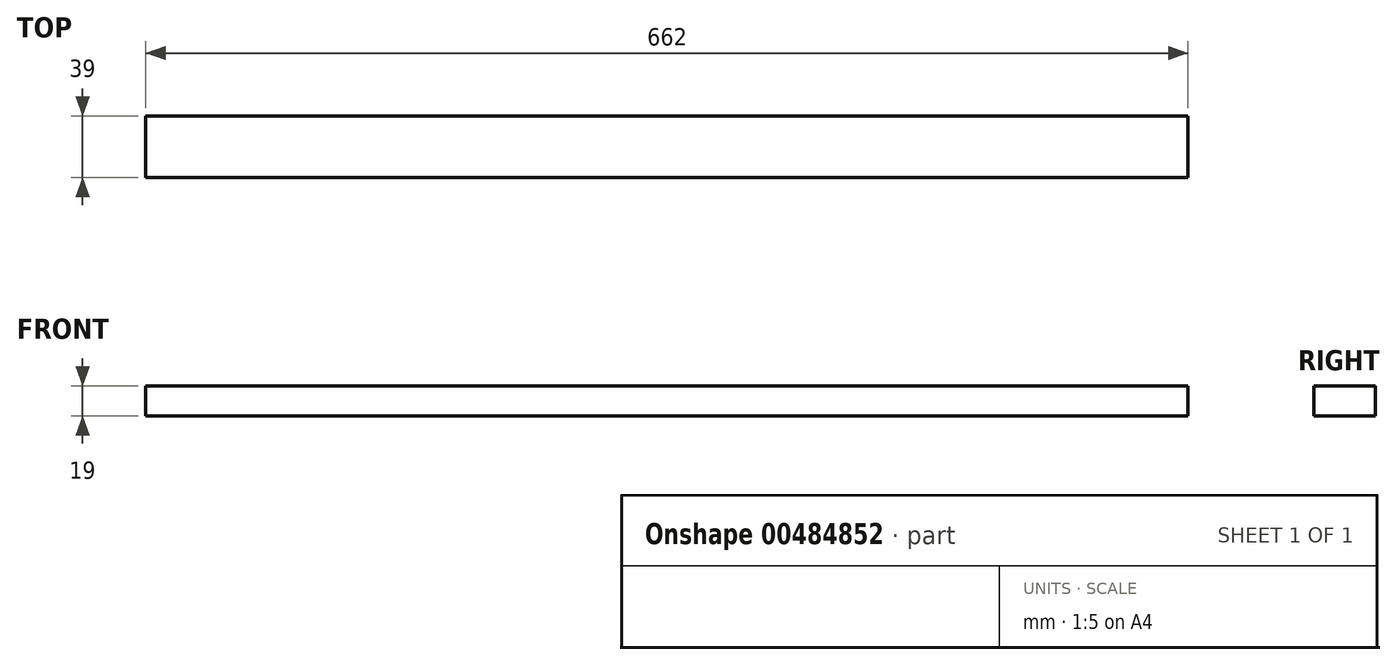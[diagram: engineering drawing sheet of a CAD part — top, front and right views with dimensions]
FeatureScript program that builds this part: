
annotation { "Feature Type Name" : "Feature", "Feature Type Description" : "" }
export const myFeature = defineFeature(function(context is Context, id is Id, definition is map)
    precondition{}
    {
        {
            var Q0;
            Q0=qCreatedBy(makeId("Top.planeOp"),FACE);
            var sketch = newSketch(context, id + "F0", { "sketchPlane" : qUnion([Q0])});
            skLineSegment(sketch, "E0.bottom", {"start": v(-202.57, 4.24) * mm, "end": v(459.43, 4.24) * mm});
            skLineSegment(sketch, "E0.top", {"start": v(-202.57, -34.76) * mm, "end": v(459.43, -34.76) * mm});
            skLineSegment(sketch, "E0.left", {"start": v(-202.57, 4.24) * mm, "end": v(-202.57, -34.76) * mm});
            skLineSegment(sketch, "E0.right", {"start": v(459.43, 4.24) * mm, "end": v(459.43, -34.76) * mm});
            skSolve(sketch);
        }
        {
            var Q0;
            Q0=makeQuery(id+"F0.imprint","IMPRINT",FACE,{"disambiguationData":[TD([[makeQuery(id+"F0.imprint","IMPRINT",EDGE,{"derivedFrom":sQuery(id+"F0.wireOp",EDGE,"E0.bottom")}),-1.0]])]});
            var Q1;
            Q1 = qSketchRegion(id + "F0", true);
            extrude(context, id + "F1", {"entities" : qUnion([Q0, Q1]), "depth" : 19 * mm});
        }
    });
